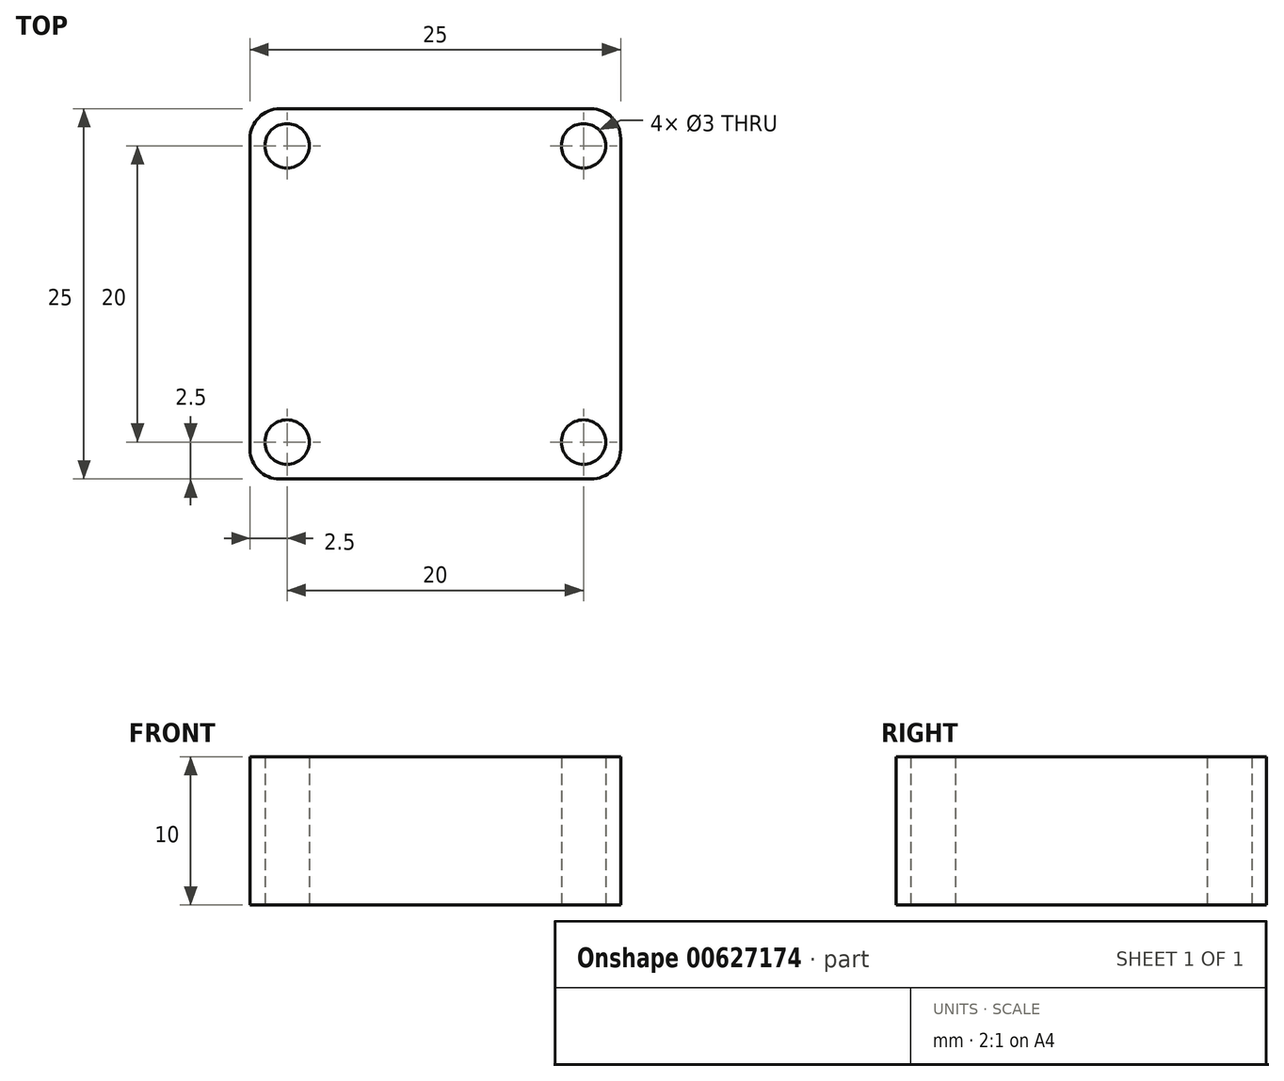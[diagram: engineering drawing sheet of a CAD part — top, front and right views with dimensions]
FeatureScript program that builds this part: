
annotation { "Feature Type Name" : "Feature", "Feature Type Description" : "" }
export const myFeature = defineFeature(function(context is Context, id is Id, definition is map)
    precondition{}
    {
        {
            var Q0;
            Q0=qCreatedBy(makeId("Top.planeOp"),FACE);
            var sketch = newSketch(context, id + "F0", { "sketchPlane" : qUnion([Q0])});
            skLineSegment(sketch, "E0.bottom", {"start": v(-12.5, 12.5) * mm, "end": v(12.5, 12.5) * mm});
            skLineSegment(sketch, "E0.top", {"start": v(-12.5, -12.5) * mm, "end": v(12.5, -12.5) * mm});
            skLineSegment(sketch, "E0.left", {"start": v(-12.5, 12.5) * mm, "end": v(-12.5, -12.5) * mm});
            skLineSegment(sketch, "E0.right", {"start": v(12.5, 12.5) * mm, "end": v(12.5, -12.5) * mm});
            skPoint(sketch, "E0.middle", {"position": v(0, 0) * mm});
            skLineSegment(sketch, "E1.bottom", {"start": v(-10, 10) * mm, "end": v(10, 10) * mm, "construction": true});
            skLineSegment(sketch, "E1.top", {"start": v(-10, -10) * mm, "end": v(10, -10) * mm, "construction": true});
            skLineSegment(sketch, "E1.left", {"start": v(-10, 10) * mm, "end": v(-10, -10) * mm, "construction": true});
            skLineSegment(sketch, "E1.right", {"start": v(10, 10) * mm, "end": v(10, -10) * mm, "construction": true});
            skCircle(sketch, "E2", {"center": v(-10, 10) * mm, "radius": 1.5 * mm});
            skCircle(sketch, "E3", {"center": v(10, 10) * mm, "radius": 1.5 * mm});
            skCircle(sketch, "E4", {"center": v(10, -10) * mm, "radius": 1.5 * mm});
            skCircle(sketch, "E5", {"center": v(-10, -10) * mm, "radius": 1.5 * mm});
            skSolve(sketch);
        }
        {
            var Q0;
            Q0=makeQuery(id+"F0.imprint","IMPRINT",FACE,{"disambiguationData":[TD([[makeQuery(id+"F0.imprint","IMPRINT",EDGE,{"derivedFrom":sQuery(id+"F0.wireOp",EDGE,"E0.bottom")}),-1.0]])]});
            extrude(context, id + "F1", {"entities" : qUnion([Q0]), "depth" : 10 * mm, "offsetDistance" : 25 * mm});
        }
        {
            var Q0;
            Q0=makeQuery(id+"F1.opExtrude","SWEPT_EDGE",EDGE,{"disambiguationData":[OSD([sQuery(id+"F0.wireOp",EDGE,"E0.top"),sQuery(id+"F0.wireOp",EDGE,"E0.left")])]});
            var Q1;
            Q1=makeQuery(id+"F1.opExtrude","SWEPT_EDGE",EDGE,{"disambiguationData":[OSD([sQuery(id+"F0.wireOp",EDGE,"E0.top"),sQuery(id+"F0.wireOp",EDGE,"E0.right")])]});
            var Q2;
            Q2=makeQuery(id+"F1.opExtrude","SWEPT_EDGE",EDGE,{"disambiguationData":[OSD([sQuery(id+"F0.wireOp",EDGE,"E0.bottom"),sQuery(id+"F0.wireOp",EDGE,"E0.right")])]});
            var Q3;
            Q3=makeQuery(id+"F1.opExtrude","SWEPT_EDGE",EDGE,{"disambiguationData":[OSD([sQuery(id+"F0.wireOp",EDGE,"E0.bottom"),sQuery(id+"F0.wireOp",EDGE,"E0.left")])]});
            fillet(context, id + "F2", {"entities" : qUnion([Q0, Q1, Q2, Q3]), "tangentPropagation" : true, "radius" : 2 * mm, "defaultsChanged" : true, "vertexSettings" : [], "allowEdgeOverflow" : false});
        }
    });
